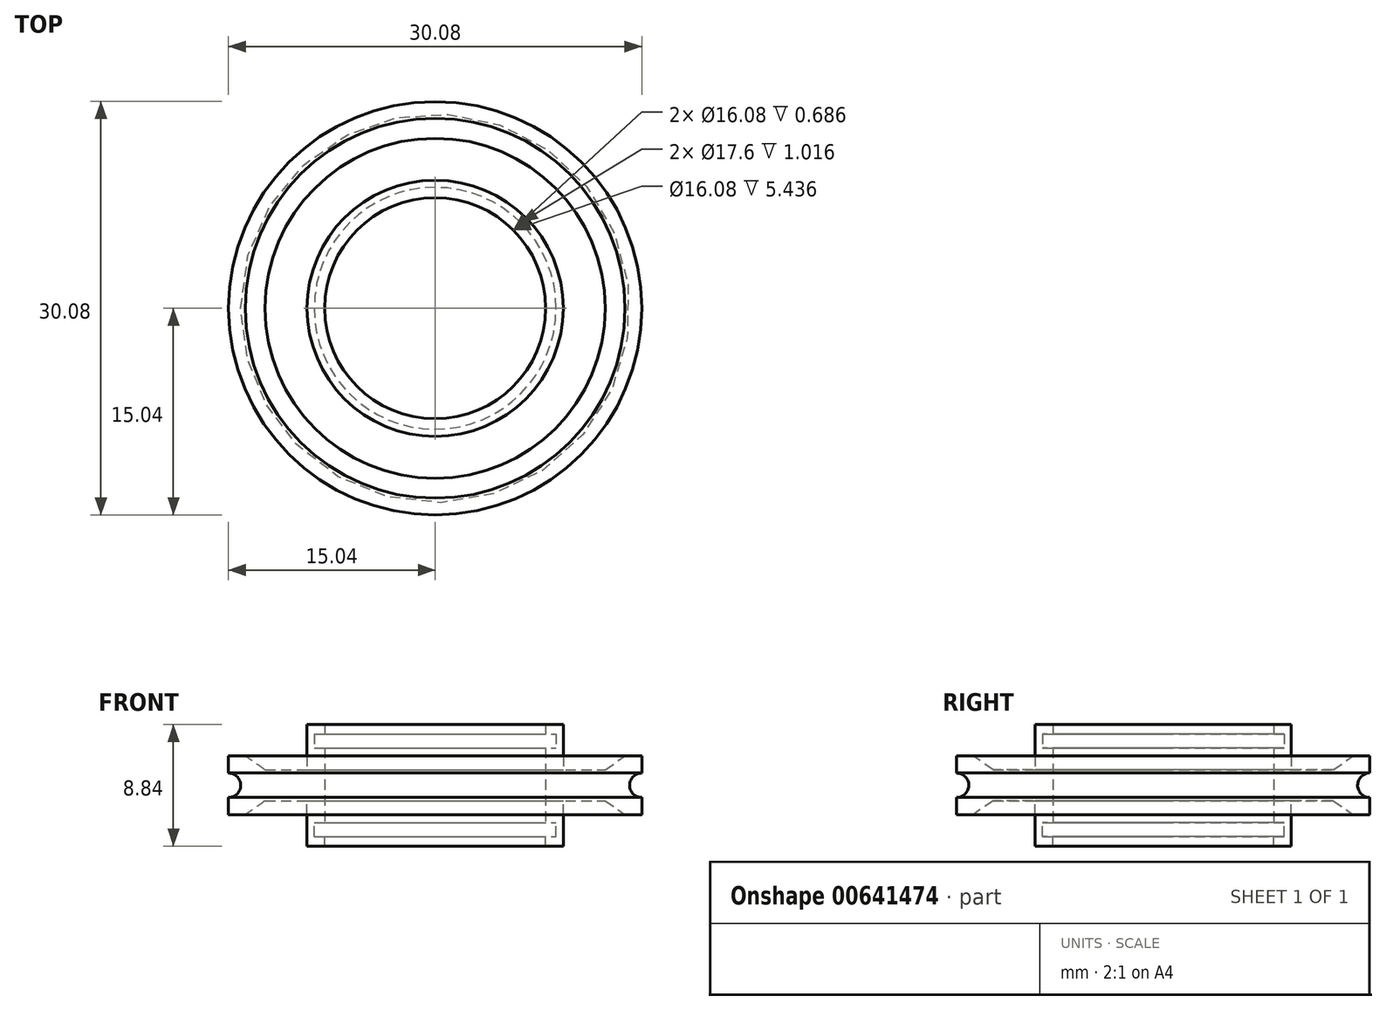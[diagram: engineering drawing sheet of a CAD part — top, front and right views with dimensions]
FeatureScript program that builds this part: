
annotation { "Feature Type Name" : "Feature", "Feature Type Description" : "" }
export const myFeature = defineFeature(function(context is Context, id is Id, definition is map)
    precondition{}
    {
        {
            var Q0;
            Q0=qCreatedBy(makeId("Front.planeOp"),FACE);
            var sketch = newSketch(context, id + "F0", { "sketchPlane" : qUnion([Q0])});
            skLineSegment(sketch, "E0", {"start": v(0, 0) * mm, "end": v(0, 39.67) * mm, "construction": true});
            skLineSegment(sketch, "E1", {"start": v(0, 0) * mm, "end": v(8.04, 0) * mm});
            skLineSegment(sketch, "E2", {"start": v(8.04, 0) * mm, "end": v(8.04, 2.72) * mm});
            skLineSegment(sketch, "E3", {"start": v(8.04, 4.42) * mm, "end": v(9.32, 4.42) * mm});
            skLineSegment(sketch, "E4", {"start": v(13.82, 2.13) * mm, "end": v(15.04, 2.13) * mm});
            skLineSegment(sketch, "E5", {"start": v(15.04, 2.13) * mm, "end": v(15.04, 0) * mm});
            skLineSegment(sketch, "E6", {"start": v(15.04, 0) * mm, "end": v(8.04, 0) * mm});
            skLineSegment(sketch, "E7", {"start": v(0, 0) * mm, "end": v(76.22, 0) * mm, "construction": true});
            skPoint(sketch, "E7.endSnap0", {"position": v(11.54, 0) * mm});
            skLineSegment(sketch, "E8", {"start": v(9.32, 4.42) * mm, "end": v(9.32, 1.12) * mm});
            skLineSegment(sketch, "E9", {"start": v(9.32, 1.12) * mm, "end": v(12.37, 1.12) * mm});
            skLineSegment(sketch, "E10", {"start": v(12.37, 1.12) * mm, "end": v(13.82, 2.13) * mm});
            skLineSegment(sketch, "E11", {"start": v(8.04, 3.73) * mm, "end": v(8.8, 3.73) * mm});
            skLineSegment(sketch, "E12", {"start": v(8.8, 3.73) * mm, "end": v(8.8, 2.72) * mm});
            skLineSegment(sketch, "E13", {"start": v(8.8, 2.72) * mm, "end": v(8.04, 2.72) * mm});
            skLineSegment(sketch, "E14.trimOffspring", {"start": v(8.04, 3.73) * mm, "end": v(8.04, 4.42) * mm});
            skSolve(sketch);
        }
        {
            var Q0;
            Q0 = qSketchRegion(id + "F0", true);
            var Q1;
            Q1=sQuery(id+"F0.wireOp",EDGE,"E0");
            revolve(context, id + "F1", {"entities" : qUnion([Q0]), "axis" : qUnion([Q1]), "revolveType" : RevolveType.FULL});
        }
        {
            var Q0;
            Q0=qCreatedBy(makeId("Front.planeOp"),FACE);
            var sketch = newSketch(context, id + "F2", { "sketchPlane" : qUnion([Q0])});
            skCircle(sketch, "E15", {"center": v(15.04, 0) * mm, "radius": 0.89 * mm});
            skSolve(sketch);
        }
        {
            var Q0;
            Q0=makeQuery(id+"F2.imprint","IMPRINT",FACE,{"disambiguationData":[TD([[makeQuery(id+"F2.imprint","IMPRINT",EDGE,{"derivedFrom":sQuery(id+"F2.wireOp",EDGE,"E15")}),1.0]])]});
            var Q1;
            Q1=sQuery(id+"F2.wireOp",EDGE,"E15");
            var Q2;
            Q2=sQuery(id+"F0.wireOp",EDGE,"E0");
            revolve(context, id + "F3", {"operationType" : NewBodyOperationType.REMOVE, "entities" : qUnion([Q0]), "surfaceEntities" : qUnion([Q1]), "axis" : qUnion([Q2]), "revolveType" : RevolveType.FULL, "oppositeDirection" : true});
        }
        {
            var Q0;
            Q0=makeQuery(id+"F1.opRevolve","SWEPT_BODY",BODY,{"disambiguationData":[OSD([sQuery(id+"F0.wireOp",EDGE,"E2"),sQuery(id+"F0.wireOp",EDGE,"E3"),sQuery(id+"F0.wireOp",EDGE,"PJkIJVYD-5Y65-tfaN-NjpZ-T8NwEgT1YXwh"),sQuery(id+"F0.wireOp",EDGE,"XjDxcdkn-iDEr-unc7-nHUf-O3jbn96MTYze"),sQuery(id+"F0.wireOp",EDGE,"zDHupnh1-PlEg-s0yY-FPZk-Z7ea7lSiXxEc"),sQuery(id+"F0.wireOp",EDGE,"E4"),sQuery(id+"F0.wireOp",EDGE,"E5"),sQuery(id+"F0.wireOp",EDGE,"E6")])]});
            var Q1;
            Q1=qCreatedBy(makeId("Top.planeOp"),FACE);
            mirror(context, id + "F4", {"operationType" : NewBodyOperationType.ADD, "entities" : qUnion([Q0]), "mirrorPlane" : qUnion([Q1])});
        }
    });
